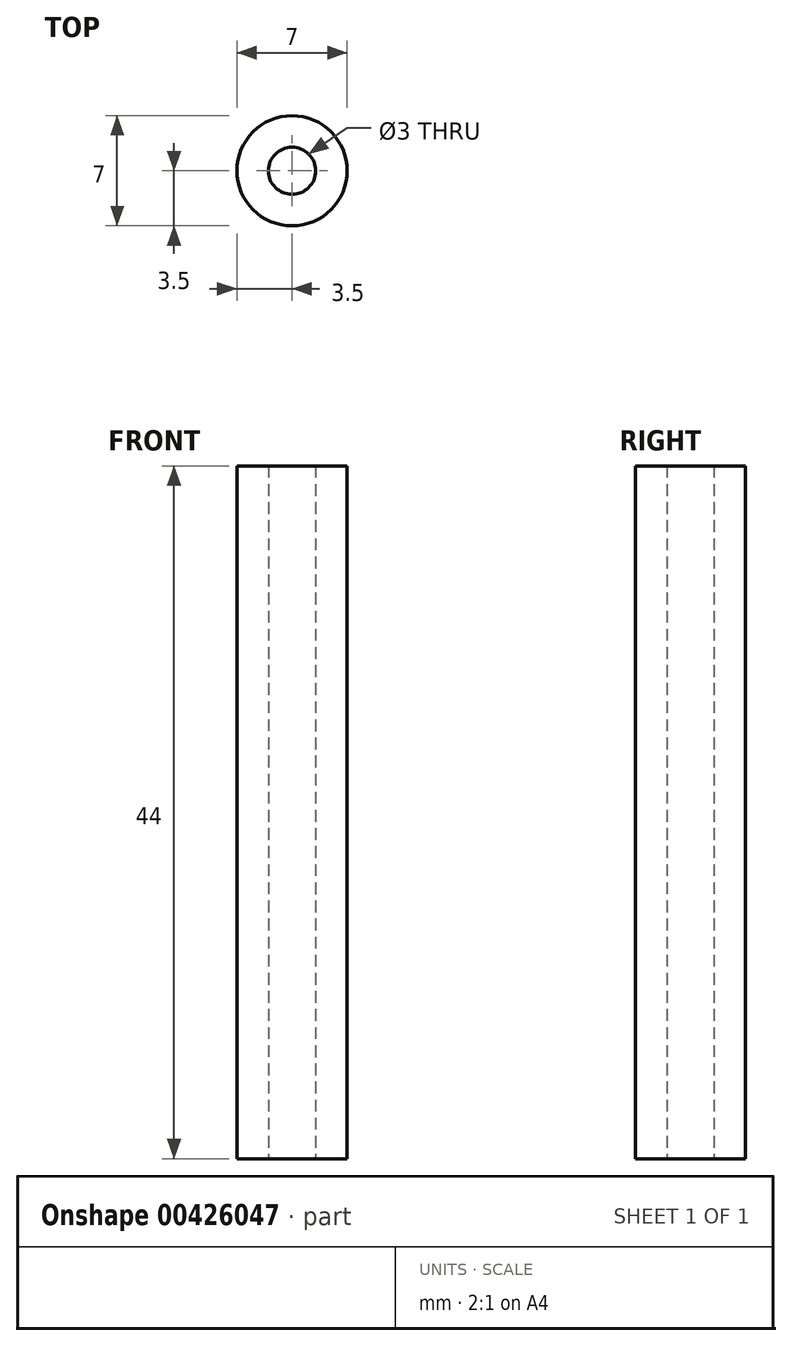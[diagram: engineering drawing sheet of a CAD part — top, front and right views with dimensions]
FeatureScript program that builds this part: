
annotation { "Feature Type Name" : "Feature", "Feature Type Description" : "" }
export const myFeature = defineFeature(function(context is Context, id is Id, definition is map)
    precondition{}
    {
        {
            var Q0;
            Q0=qCreatedBy(makeId("Top.planeOp"),FACE);
            var sketch = newSketch(context, id + "F0", { "sketchPlane" : qUnion([Q0])});
            skCircle(sketch, "E0", {"center": v(0, 0) * mm, "radius": 1.5 * mm});
            skCircle(sketch, "E1", {"center": v(0, 0) * mm, "radius": 3.5 * mm});
            skSolve(sketch);
        }
        {
            var Q0;
            Q0=makeQuery(id+"F0.imprint","IMPRINT",FACE,{"disambiguationData":[TD([[makeQuery(id+"F0.imprint","IMPRINT",EDGE,{"derivedFrom":sQuery(id+"F0.wireOp",EDGE,"E0")}),-1.0]])]});
            extrude(context, id + "F1", {"entities" : qUnion([Q0]), "depth" : 22 * mm, "hasSecondDirection" : true, "secondDirectionOppositeDirection" : true, "secondDirectionDepth" : 22 * mm});
        }
    });
